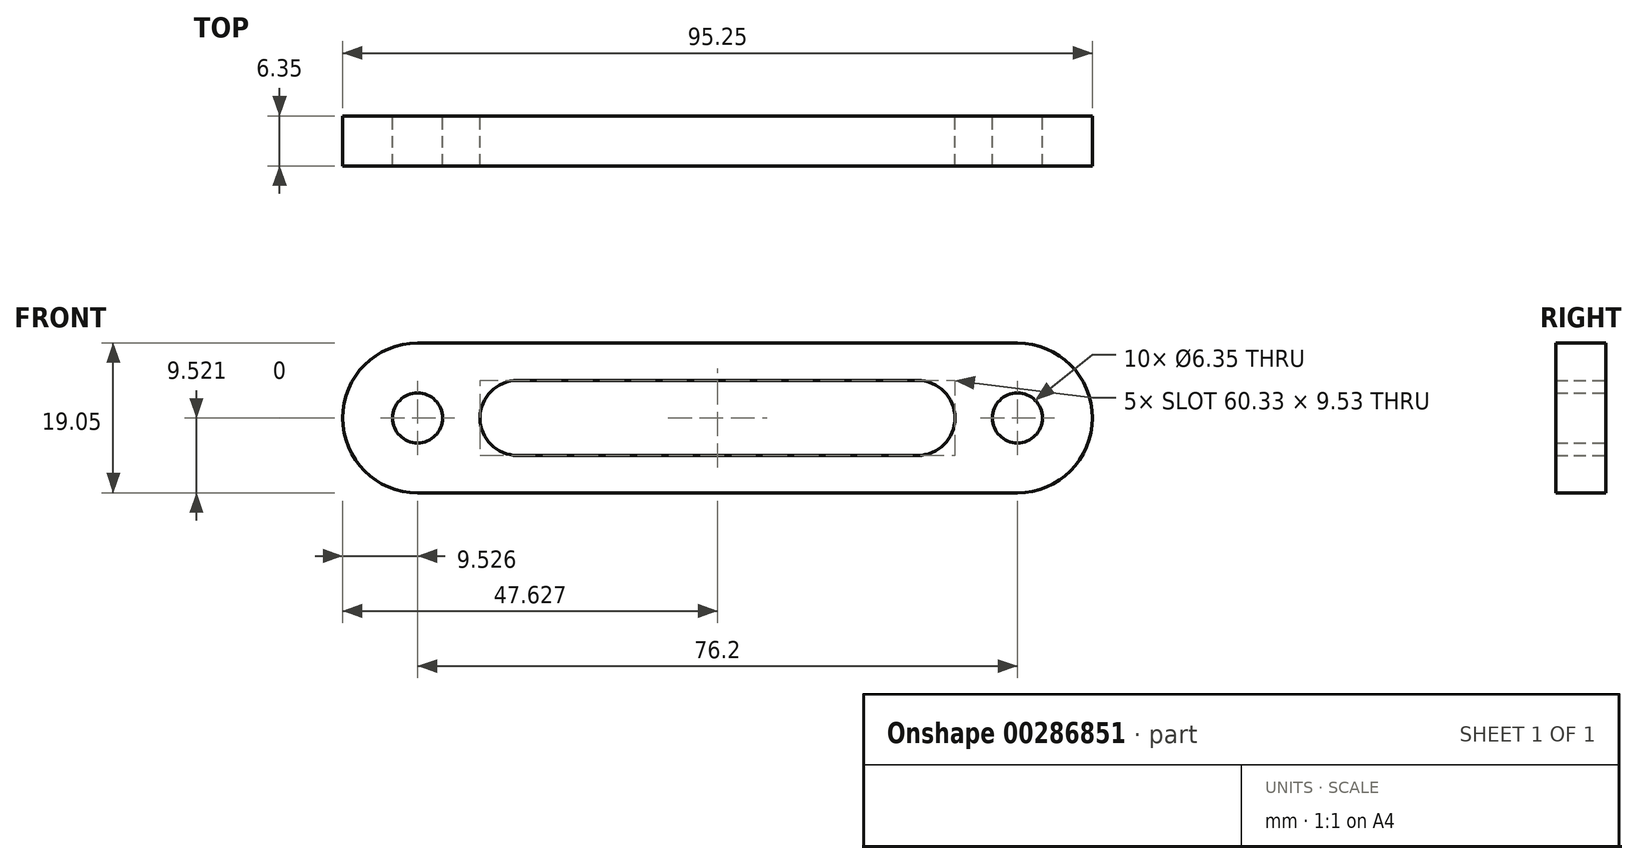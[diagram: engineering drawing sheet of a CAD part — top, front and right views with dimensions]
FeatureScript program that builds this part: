
annotation { "Feature Type Name" : "Feature", "Feature Type Description" : "" }
export const myFeature = defineFeature(function(context is Context, id is Id, definition is map)
    precondition{}
    {
        {
            var Q0;
            Q0=qCreatedBy(makeId("Front.planeOp"),FACE);
            var sketch = newSketch(context, id + "F0", { "sketchPlane" : qUnion([Q0])});
            skLineSegment(sketch, "E0.bottom", {"start": v(-36.44, 6.63) * mm, "end": v(39.76, 6.63) * mm});
            skLineSegment(sketch, "E0.top", {"start": v(-36.44, -12.42) * mm, "end": v(39.76, -12.42) * mm});
            skLineSegment(sketch, "E1.bottom", {"start": v(-23.74, 1.86) * mm, "end": v(27.06, 1.86) * mm});
            skLineSegment(sketch, "E1.top", {"start": v(-23.74, -7.66) * mm, "end": v(27.06, -7.66) * mm});
            skArc(sketch, "E2", {"start": v(-23.74, 1.86) * mm, "mid": v(-28.5, -2.9) * mm, "end": v(-23.74, -7.66) * mm});
            skArc(sketch, "E3", {"start": v(27.06, -7.66) * mm, "mid": v(31.82, -2.9) * mm, "end": v(27.06, 1.86) * mm});
            skArc(sketch, "E4", {"start": v(-36.44, 6.63) * mm, "mid": v(-45.97, -2.9) * mm, "end": v(-36.44, -12.42) * mm});
            skArc(sketch, "E5", {"start": v(39.76, -12.42) * mm, "mid": v(49.28, -2.9) * mm, "end": v(39.76, 6.63) * mm});
            skCircle(sketch, "E6", {"center": v(-36.44, -2.9) * mm, "radius": 3.18 * mm});
            skCircle(sketch, "E7", {"center": v(39.76, -2.9) * mm, "radius": 3.18 * mm});
            skSolve(sketch);
        }
        {
            var Q0;
            Q0=makeQuery(id+"F0.imprint","IMPRINT",FACE,{"disambiguationData":[TD([[makeQuery(id+"F0.imprint","IMPRINT",EDGE,{"derivedFrom":sQuery(id+"F0.wireOp",EDGE,"E0.bottom")}),-1.0]])]});
            extrude(context, id + "F1", {"entities" : qUnion([Q0]), "depth" : 6.35 * mm});
        }
    });
